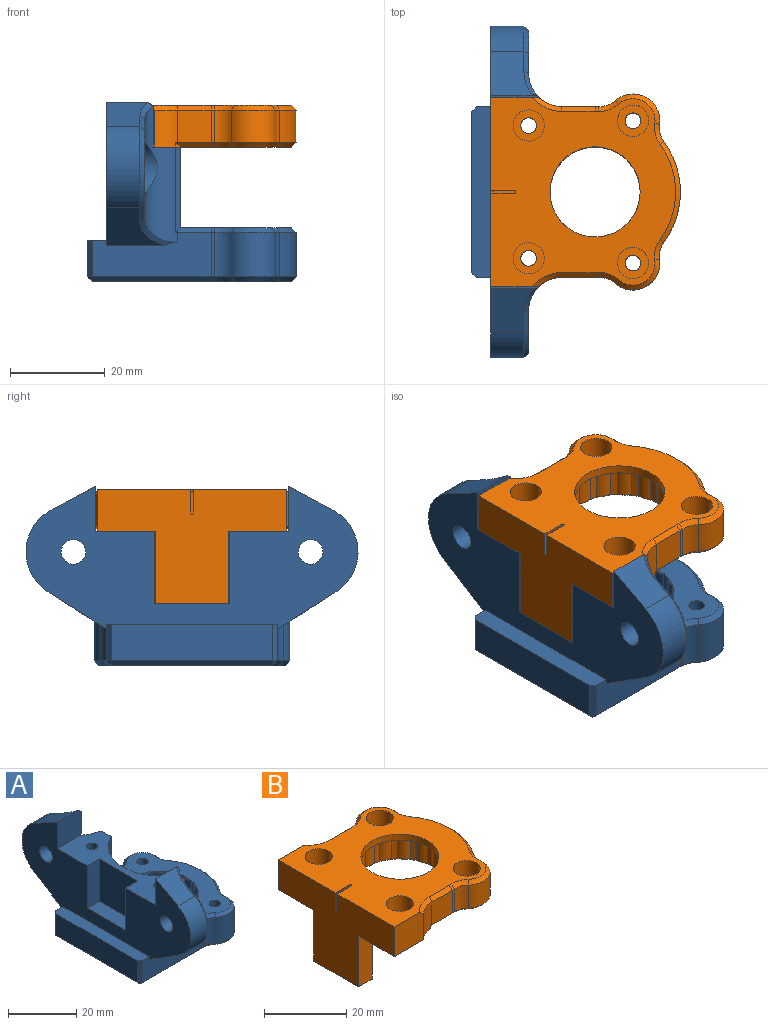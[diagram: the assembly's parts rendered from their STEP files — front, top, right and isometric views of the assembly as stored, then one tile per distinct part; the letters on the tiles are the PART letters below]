
ASSEMBLY  parts=2 mates=1
PART A: 167 faces, bbox 44.5x70.5x38.8 mm
  f0: cylinder r=11.5mm len=7mm, axis (0,0,-1), area 10.7mm2, adj f1,f24,f135,f136,f165,f166
  f1: plane 22.87x22.87mm, normal (0,0,1), area 115.8mm2, adj f0,f2,f3,f4,f5,f6,f7,f8
  f2: cylinder r=11.5mm len=7mm, axis (0,0,-1), area 10.7mm2, adj f1,f24,f163,f164,f165,f166
  f3: cylinder r=11.5mm len=7mm, axis (0,0,-1), area 10.7mm2, adj f1,f24,f161,f162,f163,f164
  f4: cylinder r=11.5mm len=7mm, axis (0,0,-1), area 10.7mm2, adj f1,f24,f159,f160,f161,f162
  f5: cylinder r=11.5mm len=7mm, axis (0,0,-1), area 10.7mm2, adj f1,f24,f157,f158,f159,f160
  f6: cylinder r=11.5mm len=7mm, axis (0,0,-1), area 10.7mm2, adj f1,f24,f155,f156,f157,f158
  f7: cylinder r=11.5mm len=7mm, axis (0,0,-1), area 10.7mm2, adj f1,f24,f153,f154,f155,f156
  f8: cylinder r=11.5mm len=7mm, axis (0,0,-1), area 10.7mm2, adj f1,f24,f151,f152,f153,f154
  f9: cylinder r=11.5mm len=7mm, axis (0,0,-1), area 10.7mm2, adj f1,f24,f149,f150,f151,f152
  f10: cylinder r=11.5mm len=7mm, axis (0,0,-1), area 10.7mm2, adj f1,f24,f147,f148,f149,f150
  f11: cylinder r=11.5mm len=7mm, axis (0,0,-1), area 10.7mm2, adj f1,f24,f145,f146,f147,f148
  f12: cylinder r=11.5mm len=7mm, axis (0,0,-1), area 10.7mm2, adj f1,f24,f143,f144,f145,f146
  f13: cylinder r=11.5mm len=7mm, axis (0,0,-1), area 10.7mm2, adj f1,f24,f141,f142,f143,f144
  f14: cylinder r=11.5mm len=7mm, axis (0,0,-1), area 10.7mm2, adj f1,f24,f139,f140,f141,f142
  f15: cylinder r=11.5mm len=7mm, axis (0,0,-1), area 10.7mm2, adj f1,f24,f137,f138,f139,f140
  f16: cylinder r=11.5mm len=7mm, axis (0,0,-1), area 10.7mm2, adj f1,f24,f135,f136,f137,f138
  f17: cylinder r=1.65mm len=22.4mm, axis (0,0,1), area 232.2mm2, adj f49,f78
  f18: plane 70x30.11mm, normal (-1,0,0), area 1084.2mm2, adj f23,f26,f28,f29,f30,f37,f78,f79
  f19: plane 17.02x3.5mm, normal (1,0,0), area 59.5mm2, adj f21,f24,f36,f61,f78
  f20: cylinder r=7mm len=28.72mm, axis (0,0,1), area 178.2mm2, adj f21,f25,f26,f40,f62,f63,f67,f68
  f21: plane 18.02x1.02mm, normal (0.73,-0.68,0), area 24mm2, adj f19,f20,f61,f62,f78
  f22: cylinder r=1.65mm len=5.4mm, axis (0,0,-1), area 56mm2, adj f24,f42
  f23: cylinder r=2.6mm len=5.2mm, axis (1,0,0), area 65.3mm2, adj f18,f39
  f24: plane 39.3x32mm, normal (0,0,1), area 488.3mm2, adj f0,f2,f3,f4,f5,f6,f7,f8
  f25: plane 20.85x9mm, normal (1,0,0), area 84.3mm2, adj f20,f40,f64,f65,f66
  f26: plane 25.5x9.9mm, normal (0,-1,0), area 190.9mm2, adj f18,f20,f30,f33,f37,f61,f63,f74
  f27: plane 42x39.3mm, normal (0,0,-1), area 992.9mm2, adj f41,f43,f44,f45,f46,f47,f48,f50
  f28: plane 9.43x8.75mm, normal (0,-0.47,0.88), area 78.1mm2, adj f18,f29,f66,f67,f68,f79
  f29: cylinder r=10mm len=17.27mm, axis (-1,0,0), area 146.1mm2, adj f18,f28,f30,f65
  f30: plane 12.36x12.32mm, normal (0,-0.53,-0.84), area 115.2mm2, adj f18,f26,f29,f63,f64
  f31: cylinder r=18mm len=21.27mm, axis (0,0,-1), area 213.9mm2, adj f34,f56,f69,f96
  f32: cylinder r=5.65mm len=9.4mm, axis (0,0,-1), area 128.9mm2, adj f34,f35,f58,f71
  f33: cylinder r=18mm len=9.4mm, axis (0,0,-1), area 7mm2, adj f26,f35,f60,f75
  f34: cylinder r=5mm len=9.4mm, axis (0,0,1), area 36mm2, adj f31,f32,f57,f70
  f35: cylinder r=5mm len=9.4mm, axis (0,0,1), area 36mm2, adj f32,f33,f59,f72
  f36: cylinder r=15mm len=27.04mm, axis (0,0,-1), area 572.5mm2, adj f19,f24,f78,f84
  f37: plane 36x4mm, normal (0,0,1), area 143mm2, adj f18,f26,f38,f74,f90,f129
  f38: plane 34x7.7mm, normal (-1,0,0), area 261.8mm2, adj f37,f73,f74,f129
  f39: plane 11x11mm, normal (1,0,0), area 73.8mm2, adj f23,f40
  f40: cylinder r=5.5mm len=11mm, axis (1,0,0), area 159.9mm2, adj f20,f25,f39
  f41: cylinder r=9.5mm len=19mm, axis (0,0,-1), area 262.6mm2, adj f1,f27
  f42: plane 6.35x5.5mm, normal (0,0,-1), area 17.6mm2, adj f22,f43,f44,f45,f46,f47,f48
  f43: plane 6x3.18mm, normal (0,-1,0), area 19.1mm2, adj f27,f42,f44,f48
  f44: plane 6x2.75mm, normal (-0.87,-0.5,0), area 19.1mm2, adj f27,f42,f43,f45
  f45: plane 6x2.75mm, normal (-0.87,0.5,0), area 19.1mm2, adj f27,f42,f44,f46
  f46: plane 6x3.18mm, normal (0,1,0), area 19.1mm2, adj f27,f42,f45,f47
  f47: plane 6x2.75mm, normal (0.87,0.5,0), area 19.1mm2, adj f27,f42,f46,f48
  f48: plane 6x2.75mm, normal (0.87,-0.5,0), area 19.1mm2, adj f27,f42,f43,f47
  f49: plane 6.35x5.5mm, normal (0,0,-1), area 17.6mm2, adj f17,f50,f51,f52,f53,f54,f55
  f50: plane 6x3.18mm, normal (0,-1,0), area 19.1mm2, adj f27,f49,f51,f55
  f51: plane 6x2.75mm, normal (-0.87,-0.5,0), area 19.1mm2, adj f27,f49,f50,f52
  f52: plane 6x2.75mm, normal (-0.87,0.5,0), area 19.1mm2, adj f27,f49,f51,f53
  f53: plane 6x3.18mm, normal (0,1,0), area 19.1mm2, adj f27,f49,f52,f54
  f54: plane 6x2.75mm, normal (0.87,0.5,0), area 19.1mm2, adj f27,f49,f53,f55
  f55: plane 6x2.75mm, normal (0.87,-0.5,0), area 19.1mm2, adj f27,f49,f50,f54
  f56: cone r=18mm half-angle=45deg, axis (0,0,-1), area 31.3mm2, adj f24,f31,f57,f114
  f57: cone r=6mm half-angle=45deg, axis (0,0,1), area 5.9mm2, adj f24,f34,f56,f58
  f58: cone r=5.65mm half-angle=45deg, axis (0,0,-1), area 17.7mm2, adj f24,f32,f57,f59
  f59: cone r=6mm half-angle=45deg, axis (0,0,1), area 5.9mm2, adj f24,f35,f58,f60
  f60: cone r=18mm half-angle=45deg, axis (0,0,-1), area 1mm2, adj f24,f33,f59,f61
  f61: plane 7x1mm, normal (0,-0.71,0.71), area 9.7mm2, adj f19,f21,f24,f26,f60,f62
  f62: cone r=7mm half-angle=45deg, axis (0,0,1), area 0.1mm2, adj f20,f21,f61
  f63: bspline ~8.63x8.06mm, area 13.7mm2, adj f20,f26,f30,f64
  f64: plane 5.35x3.89mm, normal (0.71,-0.38,-0.6), area 8.1mm2, adj f25,f30,f63,f65
  f65: cone r=9mm half-angle=45deg, axis (-1,0,0), area 28mm2, adj f25,f29,f64,f66
  f66: plane 4.71x3.14mm, normal (0.71,-0.33,0.62), area 6.8mm2, adj f25,f28,f65,f67
  f67: bspline ~5.25x3.68mm, area 7.6mm2, adj f20,f28,f66,f68
  f68: cone r=8mm half-angle=45deg, axis (0,0,1), area 0.2mm2, adj f20,f28,f67,f79
  f69: cone r=17mm half-angle=45deg, axis (0,0,1), area 31.3mm2, adj f27,f31,f70,f126
  f70: cone r=6mm half-angle=45deg, axis (0,0,-1), area 5.9mm2, adj f27,f34,f69,f71
  f71: cone r=4.65mm half-angle=45deg, axis (0,0,1), area 17.7mm2, adj f27,f32,f70,f72
  f72: cone r=6mm half-angle=45deg, axis (0,0,-1), area 5.9mm2, adj f27,f35,f71,f75
  f73: plane 34x1mm, normal (-0.71,0,-0.71), area 48.1mm2, adj f27,f38,f76,f131
  f74: plane 7.7x1mm, normal (-0.71,-0.71,0), area 10.9mm2, adj f26,f37,f38,f76
  f75: cone r=17mm half-angle=45deg, axis (0,0,1), area 1mm2, adj f27,f33,f72,f77
  f76: plane 1x1mm, normal (-0.58,-0.58,-0.58), area 0.9mm2, adj f73,f74,f77
  f77: plane 25x1mm, normal (0,-0.71,-0.71), area 35.4mm2, adj f26,f27,f75,f76
  f78: plane 40.6x15.5mm, normal (0,0,1), area 347.7mm2, adj f17,f18,f19,f20,f21,f36,f79,f80
  f79: plane 9.86x9.49mm, normal (0,1,0), area 92.2mm2, adj f18,f20,f28,f68,f78
  f80: plane 15.2x5mm, normal (0,1,0), area 76mm2, adj f18,f78,f81,f82
  f81: plane 16x15.2mm, normal (-1,0,0), area 243.2mm2, adj f78,f80,f82,f134
  f82: plane 16x5mm, normal (0,0,1), area 80mm2, adj f18,f80,f81,f134
  f83: cylinder r=1.65mm len=22.4mm, axis (0,0,1), area 232.2mm2, adj f78,f107
  f84: plane 17.02x3.5mm, normal (1,0,0), area 59.5mm2, adj f24,f36,f78,f86,f118
  f85: cylinder r=7mm len=28.72mm, axis (0,0,1), area 178.2mm2, adj f78,f86,f89,f90,f99,f119,f120,f124
  f86: plane 18.02x1.02mm, normal (0.73,0.68,0), area 24mm2, adj f78,f84,f85,f118,f119
  f87: cylinder r=1.65mm len=5.4mm, axis (0,0,-1), area 56mm2, adj f24,f100
  f88: cylinder r=2.6mm len=5.2mm, axis (1,0,0), area 65.3mm2, adj f18,f98
  f89: plane 20.85x9mm, normal (1,0,0), area 84.3mm2, adj f85,f99,f121,f122,f123
  f90: plane 25.5x9.9mm, normal (0,1,0), area 190.9mm2, adj f18,f37,f85,f93,f95,f118,f120,f129
  f91: plane 9.43x8.75mm, normal (0,0.47,0.88), area 78.1mm2, adj f18,f92,f123,f124,f125,f133
  f92: cylinder r=10mm len=17.27mm, axis (-1,0,0), area 146.1mm2, adj f18,f91,f93,f122
  f93: plane 12.36x12.32mm, normal (0,0.53,-0.84), area 115.2mm2, adj f18,f90,f92,f120,f121
  f94: cylinder r=5.65mm len=9.4mm, axis (0,0,-1), area 128.9mm2, adj f96,f97,f115,f127
  f95: cylinder r=18mm len=9.4mm, axis (0,0,-1), area 7mm2, adj f90,f97,f117,f130
  f96: cylinder r=5mm len=9.4mm, axis (0,0,1), area 36mm2, adj f31,f94,f114,f126
  f97: cylinder r=5mm len=9.4mm, axis (0,0,1), area 36mm2, adj f94,f95,f116,f128
  f98: plane 11x11mm, normal (1,0,0), area 73.8mm2, adj f88,f99
  f99: cylinder r=5.5mm len=11mm, axis (1,0,0), area 159.9mm2, adj f85,f89,f98
  f100: plane 6.35x5.5mm, normal (0,0,-1), area 17.6mm2, adj f87,f101,f102,f103,f104,f105,f106
  f101: plane 6x3.18mm, normal (0,1,0), area 19.1mm2, adj f27,f100,f102,f106
  f102: plane 6x2.75mm, normal (-0.87,0.5,0), area 19.1mm2, adj f27,f100,f101,f103
  f103: plane 6x2.75mm, normal (-0.87,-0.5,0), area 19.1mm2, adj f27,f100,f102,f104
  f104: plane 6x3.18mm, normal (0,-1,0), area 19.1mm2, adj f27,f100,f103,f105
  f105: plane 6x2.75mm, normal (0.87,-0.5,0), area 19.1mm2, adj f27,f100,f104,f106
  f106: plane 6x2.75mm, normal (0.87,0.5,0), area 19.1mm2, adj f27,f100,f101,f105
  f107: plane 6.35x5.5mm, normal (0,0,-1), area 17.6mm2, adj f83,f108,f109,f110,f111,f112,f113
  f108: plane 6x3.18mm, normal (0,1,0), area 19.1mm2, adj f27,f107,f109,f113
  f109: plane 6x2.75mm, normal (-0.87,0.5,0), area 19.1mm2, adj f27,f107,f108,f110
  f110: plane 6x2.75mm, normal (-0.87,-0.5,0), area 19.1mm2, adj f27,f107,f109,f111
  f111: plane 6x3.18mm, normal (0,-1,0), area 19.1mm2, adj f27,f107,f110,f112
  f112: plane 6x2.75mm, normal (0.87,-0.5,0), area 19.1mm2, adj f27,f107,f111,f113
  f113: plane 6x2.75mm, normal (0.87,0.5,0), area 19.1mm2, adj f27,f107,f108,f112
  f114: cone r=6mm half-angle=45deg, axis (0,0,1), area 5.9mm2, adj f24,f56,f96,f115
  f115: cone r=5.65mm half-angle=45deg, axis (0,0,-1), area 17.7mm2, adj f24,f94,f114,f116
  f116: cone r=6mm half-angle=45deg, axis (0,0,1), area 5.9mm2, adj f24,f97,f115,f117
  f117: cone r=18mm half-angle=45deg, axis (0,0,-1), area 1mm2, adj f24,f95,f116,f118
  f118: plane 7x1mm, normal (0,0.71,0.71), area 9.7mm2, adj f24,f84,f86,f90,f117,f119
  f119: cone r=7mm half-angle=45deg, axis (0,0,1), area 0.1mm2, adj f85,f86,f118
  f120: bspline ~8.63x8.06mm, area 13.7mm2, adj f85,f90,f93,f121
  f121: plane 5.35x3.89mm, normal (0.71,0.38,-0.6), area 8.1mm2, adj f89,f93,f120,f122
  f122: cone r=9mm half-angle=45deg, axis (-1,0,0), area 28mm2, adj f89,f92,f121,f123
  f123: plane 4.71x3.14mm, normal (0.71,0.33,0.62), area 6.8mm2, adj f89,f91,f122,f124
  f124: bspline ~6.1x4.14mm, area 7.6mm2, adj f85,f91,f123,f125
  f125: cone r=8mm half-angle=45deg, axis (0,0,1), area 0.2mm2, adj f85,f91,f124,f133
  f126: cone r=6mm half-angle=45deg, axis (0,0,-1), area 5.9mm2, adj f27,f69,f96,f127
  f127: cone r=4.65mm half-angle=45deg, axis (0,0,1), area 17.7mm2, adj f27,f94,f126,f128
  f128: cone r=6mm half-angle=45deg, axis (0,0,-1), area 5.9mm2, adj f27,f97,f127,f130
  f129: plane 7.7x1mm, normal (-0.71,0.71,0), area 10.9mm2, adj f37,f38,f90,f131
  f130: cone r=17mm half-angle=45deg, axis (0,0,1), area 1mm2, adj f27,f95,f128,f132
  f131: plane 1x1mm, normal (-0.58,0.58,-0.58), area 0.9mm2, adj f73,f129,f132
  f132: plane 25x1mm, normal (0,0.71,-0.71), area 35.4mm2, adj f27,f90,f130,f131
  f133: plane 9.86x9.49mm, normal (0,-1,0), area 92.2mm2, adj f18,f78,f85,f91,f125
  f134: plane 15.2x5mm, normal (0,-1,0), area 76mm2, adj f18,f78,f81,f82
  f135: cylinder r=3mm len=6.7mm, axis (0,0,-1), area 21mm2, adj f0,f1,f16,f136
  f136: cone r=2.7mm half-angle=45deg, axis (0,0,-1), area 1.1mm2, adj f0,f16,f24,f135
  f137: cylinder r=3mm len=6.7mm, axis (0,0,-1), area 21mm2, adj f1,f15,f16,f138
  f138: cone r=2.7mm half-angle=45deg, axis (0,0,-1), area 1.1mm2, adj f15,f16,f24,f137
  f139: cylinder r=3mm len=6.7mm, axis (0,0,-1), area 21mm2, adj f1,f14,f15,f140
  f140: cone r=2.7mm half-angle=45deg, axis (0,0,-1), area 1.1mm2, adj f14,f15,f24,f139
  f141: cylinder r=3mm len=6.7mm, axis (0,0,-1), area 21mm2, adj f1,f13,f14,f142
  f142: cone r=2.7mm half-angle=45deg, axis (0,0,-1), area 1.1mm2, adj f13,f14,f24,f141
  f143: cylinder r=3mm len=6.7mm, axis (0,0,-1), area 21mm2, adj f1,f12,f13,f144
  f144: cone r=2.7mm half-angle=45deg, axis (0,0,-1), area 1.1mm2, adj f12,f13,f24,f143
  f145: cylinder r=3mm len=6.7mm, axis (0,0,-1), area 21mm2, adj f1,f11,f12,f146
  f146: cone r=2.7mm half-angle=45deg, axis (0,0,-1), area 1.1mm2, adj f11,f12,f24,f145
  f147: cylinder r=3mm len=6.7mm, axis (0,0,-1), area 21mm2, adj f1,f10,f11,f148
  f148: cone r=2.7mm half-angle=45deg, axis (0,0,-1), area 1.1mm2, adj f10,f11,f24,f147
  f149: cylinder r=3mm len=6.7mm, axis (0,0,-1), area 21mm2, adj f1,f9,f10,f150
  f150: cone r=2.7mm half-angle=45deg, axis (0,0,-1), area 1.1mm2, adj f9,f10,f24,f149
  f151: cylinder r=3mm len=6.7mm, axis (0,0,-1), area 21mm2, adj f1,f8,f9,f152
  f152: cone r=2.7mm half-angle=45deg, axis (0,0,-1), area 1.1mm2, adj f8,f9,f24,f151
  f153: cylinder r=3mm len=6.7mm, axis (0,0,-1), area 21mm2, adj f1,f7,f8,f154
  f154: cone r=2.7mm half-angle=45deg, axis (0,0,-1), area 1.1mm2, adj f7,f8,f24,f153
  f155: cylinder r=3mm len=6.7mm, axis (0,0,-1), area 21mm2, adj f1,f6,f7,f156
  f156: cone r=2.7mm half-angle=45deg, axis (0,0,-1), area 1.1mm2, adj f6,f7,f24,f155
  f157: cylinder r=3mm len=6.7mm, axis (0,0,-1), area 21mm2, adj f1,f5,f6,f158
  f158: cone r=2.7mm half-angle=45deg, axis (0,0,-1), area 1.1mm2, adj f5,f6,f24,f157
  f159: cylinder r=3mm len=6.7mm, axis (0,0,-1), area 21mm2, adj f1,f4,f5,f160
  f160: cone r=2.7mm half-angle=45deg, axis (0,0,-1), area 1.1mm2, adj f4,f5,f24,f159
  f161: cylinder r=3mm len=6.7mm, axis (0,0,-1), area 21mm2, adj f1,f3,f4,f162
  f162: cone r=2.7mm half-angle=45deg, axis (0,0,-1), area 1.1mm2, adj f3,f4,f24,f161
  f163: cylinder r=3mm len=6.7mm, axis (0,0,-1), area 21mm2, adj f1,f2,f3,f164
  f164: cone r=2.7mm half-angle=45deg, axis (0,0,-1), area 1.1mm2, adj f2,f3,f24,f163
  f165: cylinder r=3mm len=6.7mm, axis (0,0,-1), area 21mm2, adj f0,f1,f2,f166
  f166: cone r=2.7mm half-angle=45deg, axis (0,0,-1), area 1.1mm2, adj f0,f2,f24,f165
PART B: 120 faces, bbox 40x41.3x24 mm
  f0: plane 40x39mm, normal (0,0,1), area 919.6mm2, adj f18,f32,f34,f36,f44,f45,f46,f47
  f1: plane 4.8x0.6mm, normal (-1,0,0), area 2.8mm2, adj f115,f116,f117,f119
  f2: cylinder r=11.5mm len=7mm, axis (0,0,-1), area 10.7mm2, adj f24,f31,f111,f112,f113,f114
  f3: cylinder r=11.5mm len=7mm, axis (0,0,-1), area 10.7mm2, adj f24,f31,f109,f110,f111,f112
  f4: cylinder r=11.5mm len=7mm, axis (0,0,-1), area 10.7mm2, adj f24,f31,f107,f108,f109,f110
  f5: cylinder r=11.5mm len=7mm, axis (0,0,-1), area 10.7mm2, adj f24,f31,f105,f106,f107,f108
  f6: cylinder r=11.5mm len=7mm, axis (0,0,-1), area 10.7mm2, adj f24,f31,f103,f104,f105,f106
  f7: cylinder r=11.5mm len=7mm, axis (0,0,-1), area 10.7mm2, adj f24,f31,f101,f102,f103,f104
  f8: cylinder r=11.5mm len=7mm, axis (0,0,-1), area 10.7mm2, adj f24,f31,f99,f100,f101,f102
  f9: cylinder r=11.5mm len=7mm, axis (0,0,-1), area 10.7mm2, adj f24,f31,f97,f98,f99,f100
  f10: cylinder r=11.5mm len=7mm, axis (0,0,-1), area 10.7mm2, adj f24,f31,f95,f96,f97,f98
  f11: cylinder r=11.5mm len=7mm, axis (0,0,-1), area 10.7mm2, adj f24,f31,f93,f94,f95,f96
  f12: cylinder r=11.5mm len=7mm, axis (0,0,-1), area 10.7mm2, adj f24,f31,f91,f92,f93,f94
  f13: cylinder r=11.5mm len=7mm, axis (0,0,-1), area 10.7mm2, adj f24,f31,f89,f90,f91,f92
  f14: cylinder r=11.5mm len=7mm, axis (0,0,-1), area 10.7mm2, adj f24,f31,f87,f88,f89,f90
  f15: cylinder r=11.5mm len=7mm, axis (0,0,-1), area 10.7mm2, adj f24,f31,f85,f86,f87,f88
  f16: cylinder r=11.5mm len=7mm, axis (0,0,-1), area 10.7mm2, adj f24,f31,f83,f84,f85,f86
  f17: cylinder r=1.65mm len=3.3mm, axis (0,0,1), area 29mm2, adj f24,f33
  f18: plane 40x24mm, normal (-1,0,0), area 582.9mm2, adj f0,f24,f51,f52,f54,f81,f82,f115
  f19: plane 0.02x0.02mm, normal (1,0,0), area 0mm2, adj f21,f24,f38
  f20: cylinder r=7mm len=7.8mm, axis (0,0,1), area 41.9mm2, adj f21,f22,f24,f37,f44,f51
  f21: plane 1.02x1.02mm, normal (0.73,-0.68,0), area 0.7mm2, adj f19,f20,f24,f37,f38
  f22: plane 7x6.8mm, normal (0,-1,0), area 47.6mm2, adj f20,f28,f38,f45
  f23: cylinder r=1.65mm len=3.3mm, axis (0,0,-1), area 29mm2, adj f24,f35
  f24: plane 40x39mm, normal (0,0,-1), area 837.7mm2, adj f2,f3,f4,f5,f6,f7,f8,f9
  f25: cylinder r=11.5mm len=7mm, axis (0,0,-1), area 10.7mm2, adj f24,f31,f83,f84,f113,f114
  f26: cylinder r=18mm len=21.27mm, axis (0,0,-1), area 154.7mm2, adj f29,f43,f50,f63
  f27: cylinder r=5.65mm len=9.39mm, axis (0,0,-1), area 93.3mm2, adj f29,f30,f41,f48
  f28: cylinder r=18mm len=6.8mm, axis (0,0,-1), area 5mm2, adj f22,f30,f39,f46
  f29: cylinder r=5mm len=6.8mm, axis (0,0,1), area 26mm2, adj f26,f27,f42,f49
  f30: cylinder r=5mm len=6.8mm, axis (0,0,1), area 26mm2, adj f27,f28,f40,f47
  f31: plane 22.98x22.98mm, normal (0,0,-1), area 115.8mm2, adj f2,f3,f4,f5,f6,f7,f8,f9
  f32: cylinder r=9.5mm len=19mm, axis (0,0,1), area 107.4mm2, adj f0,f31
  f33: plane 6.6x6.6mm, normal (0,0,1), area 25.7mm2, adj f17,f34
  f34: cylinder r=3.3mm len=6.6mm, axis (0,0,1), area 124.4mm2, adj f0,f33
  f35: plane 6.6x6.6mm, normal (0,0,1), area 25.7mm2, adj f23,f36
  f36: cylinder r=3.3mm len=6.6mm, axis (0,0,1), area 124.4mm2, adj f0,f35
  f37: cone r=8mm half-angle=45deg, axis (0,0,-1), area 0.1mm2, adj f20,f21,f38
  f38: plane 7x1mm, normal (0,-0.71,-0.71), area 9.7mm2, adj f19,f21,f22,f24,f37,f39
  f39: cone r=17mm half-angle=45deg, axis (0,0,1), area 1mm2, adj f24,f28,f38,f40
  f40: cone r=6mm half-angle=45deg, axis (0,0,-1), area 5.9mm2, adj f24,f30,f39,f41
  f41: cone r=4.65mm half-angle=45deg, axis (0,0,1), area 17.7mm2, adj f24,f27,f40,f42
  f42: cone r=6mm half-angle=45deg, axis (0,0,-1), area 5.9mm2, adj f24,f29,f41,f43
  f43: cone r=17mm half-angle=45deg, axis (0,0,1), area 31.3mm2, adj f24,f26,f42,f74
  f44: cone r=8mm half-angle=45deg, axis (0,0,1), area 8.9mm2, adj f0,f20,f45,f51
  f45: plane 7x1mm, normal (0,-0.71,0.71), area 9.9mm2, adj f0,f22,f44,f46
  f46: cone r=18mm half-angle=45deg, axis (0,0,-1), area 1mm2, adj f0,f28,f45,f47
  f47: cone r=6mm half-angle=45deg, axis (0,0,1), area 5.9mm2, adj f0,f30,f46,f48
  f48: cone r=5.65mm half-angle=45deg, axis (0,0,-1), area 17.7mm2, adj f0,f27,f47,f49
  f49: cone r=6mm half-angle=45deg, axis (0,0,1), area 5.9mm2, adj f0,f29,f48,f50
  f50: cone r=18mm half-angle=45deg, axis (0,0,-1), area 31.3mm2, adj f0,f26,f49,f80
  f51: plane 10.1x8.8mm, normal (0,-1,0), area 88.2mm2, adj f0,f18,f20,f24,f44
  f52: plane 15.2x4.7mm, normal (0,-1,0), area 71.4mm2, adj f18,f24,f53,f54
  f53: plane 15.4x15.2mm, normal (1,0,0), area 234.1mm2, adj f24,f52,f54,f82
  f54: plane 15.4x4.7mm, normal (0,0,-1), area 72.4mm2, adj f18,f52,f53,f82
  f55: cylinder r=1.65mm len=3.3mm, axis (0,0,1), area 29mm2, adj f24,f65
  f56: plane 0.02x0.02mm, normal (1,0,0), area 0mm2, adj f24,f58,f70
  f57: cylinder r=7mm len=7.8mm, axis (0,0,1), area 41.9mm2, adj f24,f58,f59,f69,f75,f81
  f58: plane 1.02x1.02mm, normal (0.73,0.68,0), area 0.7mm2, adj f24,f56,f57,f69,f70
  f59: plane 7x6.8mm, normal (0,1,0), area 47.6mm2, adj f57,f62,f70,f76
  f60: cylinder r=1.65mm len=3.3mm, axis (0,0,-1), area 29mm2, adj f24,f67
  f61: cylinder r=5.65mm len=9.39mm, axis (0,0,-1), area 93.3mm2, adj f63,f64,f73,f79
  f62: cylinder r=18mm len=6.8mm, axis (0,0,-1), area 5mm2, adj f59,f64,f71,f77
  f63: cylinder r=5mm len=6.8mm, axis (0,0,1), area 26mm2, adj f26,f61,f74,f80
  f64: cylinder r=5mm len=6.8mm, axis (0,0,1), area 26mm2, adj f61,f62,f72,f78
  f65: plane 6.6x6.6mm, normal (0,0,1), area 25.7mm2, adj f55,f66
  f66: cylinder r=3.3mm len=6.6mm, axis (0,0,1), area 124.4mm2, adj f0,f65
  f67: plane 6.6x6.6mm, normal (0,0,1), area 25.7mm2, adj f60,f68
  f68: cylinder r=3.3mm len=6.6mm, axis (0,0,1), area 124.4mm2, adj f0,f67
  f69: cone r=8mm half-angle=45deg, axis (0,0,-1), area 0.1mm2, adj f57,f58,f70
  f70: plane 7x1mm, normal (0,0.71,-0.71), area 9.7mm2, adj f24,f56,f58,f59,f69,f71
  f71: cone r=17mm half-angle=45deg, axis (0,0,1), area 1mm2, adj f24,f62,f70,f72
  f72: cone r=6mm half-angle=45deg, axis (0,0,-1), area 5.9mm2, adj f24,f64,f71,f73
  f73: cone r=4.65mm half-angle=45deg, axis (0,0,1), area 17.7mm2, adj f24,f61,f72,f74
  f74: cone r=6mm half-angle=45deg, axis (0,0,-1), area 5.9mm2, adj f24,f43,f63,f73
  f75: cone r=8mm half-angle=45deg, axis (0,0,1), area 8.9mm2, adj f0,f57,f76,f81
  f76: plane 7x1mm, normal (0,0.71,0.71), area 9.9mm2, adj f0,f59,f75,f77
  f77: cone r=18mm half-angle=45deg, axis (0,0,-1), area 1mm2, adj f0,f62,f76,f78
  f78: cone r=6mm half-angle=45deg, axis (0,0,1), area 5.9mm2, adj f0,f64,f77,f79
  f79: cone r=5.65mm half-angle=45deg, axis (0,0,-1), area 17.7mm2, adj f0,f61,f78,f80
  f80: cone r=6mm half-angle=45deg, axis (0,0,1), area 5.9mm2, adj f0,f50,f63,f79
  f81: plane 10.1x8.8mm, normal (0,1,0), area 88.2mm2, adj f0,f18,f24,f57,f75
  f82: plane 15.2x4.7mm, normal (0,1,0), area 71.4mm2, adj f18,f24,f53,f54
  f83: cylinder r=3mm len=6.7mm, axis (0,0,1), area 21mm2, adj f16,f25,f31,f84
  f84: cone r=3mm half-angle=45deg, axis (0,0,1), area 1.1mm2, adj f16,f24,f25,f83
  f85: cylinder r=3mm len=6.7mm, axis (0,0,1), area 21mm2, adj f15,f16,f31,f86
  f86: cone r=3mm half-angle=45deg, axis (0,0,1), area 1.1mm2, adj f15,f16,f24,f85
  f87: cylinder r=3mm len=6.7mm, axis (0,0,1), area 21mm2, adj f14,f15,f31,f88
  f88: cone r=3mm half-angle=45deg, axis (0,0,1), area 1.1mm2, adj f14,f15,f24,f87
  f89: cylinder r=3mm len=6.7mm, axis (0,0,1), area 21mm2, adj f13,f14,f31,f90
  f90: cone r=3mm half-angle=45deg, axis (0,0,1), area 1.1mm2, adj f13,f14,f24,f89
  f91: cylinder r=3mm len=6.7mm, axis (0,0,1), area 21mm2, adj f12,f13,f31,f92
  f92: cone r=3mm half-angle=45deg, axis (0,0,1), area 1.1mm2, adj f12,f13,f24,f91
  f93: cylinder r=3mm len=6.7mm, axis (0,0,1), area 21mm2, adj f11,f12,f31,f94
  f94: cone r=3mm half-angle=45deg, axis (0,0,1), area 1.1mm2, adj f11,f12,f24,f93
  f95: cylinder r=3mm len=6.7mm, axis (0,0,1), area 21mm2, adj f10,f11,f31,f96
  f96: cone r=3mm half-angle=45deg, axis (0,0,1), area 1.1mm2, adj f10,f11,f24,f95
  f97: cylinder r=3mm len=6.7mm, axis (0,0,1), area 21mm2, adj f9,f10,f31,f98
  f98: cone r=3mm half-angle=45deg, axis (0,0,1), area 1.1mm2, adj f9,f10,f24,f97
  f99: cylinder r=3mm len=6.7mm, axis (0,0,1), area 21mm2, adj f8,f9,f31,f100
  f100: cone r=3mm half-angle=45deg, axis (0,0,1), area 1.1mm2, adj f8,f9,f24,f99
  f101: cylinder r=3mm len=6.7mm, axis (0,0,1), area 21mm2, adj f7,f8,f31,f102
  f102: cone r=3mm half-angle=45deg, axis (0,0,1), area 1.1mm2, adj f7,f8,f24,f101
  f103: cylinder r=3mm len=6.7mm, axis (0,0,1), area 21mm2, adj f6,f7,f31,f104
  f104: cone r=3mm half-angle=45deg, axis (0,0,1), area 1.1mm2, adj f6,f7,f24,f103
  f105: cylinder r=3mm len=6.7mm, axis (0,0,1), area 21mm2, adj f5,f6,f31,f106
  f106: cone r=3mm half-angle=45deg, axis (0,0,1), area 1.1mm2, adj f5,f6,f24,f105
  f107: cylinder r=3mm len=6.7mm, axis (0,0,1), area 21mm2, adj f4,f5,f31,f108
  f108: cone r=3mm half-angle=45deg, axis (0,0,1), area 1.1mm2, adj f4,f5,f24,f107
  f109: cylinder r=3mm len=6.7mm, axis (0,0,1), area 21mm2, adj f3,f4,f31,f110
  f110: cone r=3mm half-angle=45deg, axis (0,0,1), area 1.1mm2, adj f3,f4,f24,f109
  f111: cylinder r=3mm len=6.7mm, axis (0,0,1), area 21mm2, adj f2,f3,f31,f112
  f112: cone r=3mm half-angle=45deg, axis (0,0,1), area 1.1mm2, adj f2,f3,f24,f111
  f113: cylinder r=3mm len=6.7mm, axis (0,0,1), area 21mm2, adj f2,f25,f31,f114
  f114: cone r=3mm half-angle=45deg, axis (0,0,1), area 1.1mm2, adj f2,f24,f25,f113
  f115: plane 5x5mm, normal (0,-1,0), area 4.8mm2, adj f0,f1,f18,f116,f118,f119
  f116: cylinder r=0.3mm len=0.6mm, axis (-1,0,0), area 0.5mm2, adj f1,f18,f115,f117
  f117: plane 5x5mm, normal (0,1,0), area 4.8mm2, adj f0,f1,f18,f116,f118,f119
  f118: cylinder r=0.3mm len=0.6mm, axis (0,0,1), area 0.5mm2, adj f0,f115,f117,f119
  f119: plane 4.8x0.6mm, normal (0,0,1), area 2.8mm2, adj f1,f115,f117,f118
PLACE A t=(78.21,105.62,0.88)mm fixed
PLACE B t=(78.21,105.62,0.08)mm
MATE fastened A.f83 <-> B.f55  axis (0,0,1) through (86.21,119.62,20.28)mm
